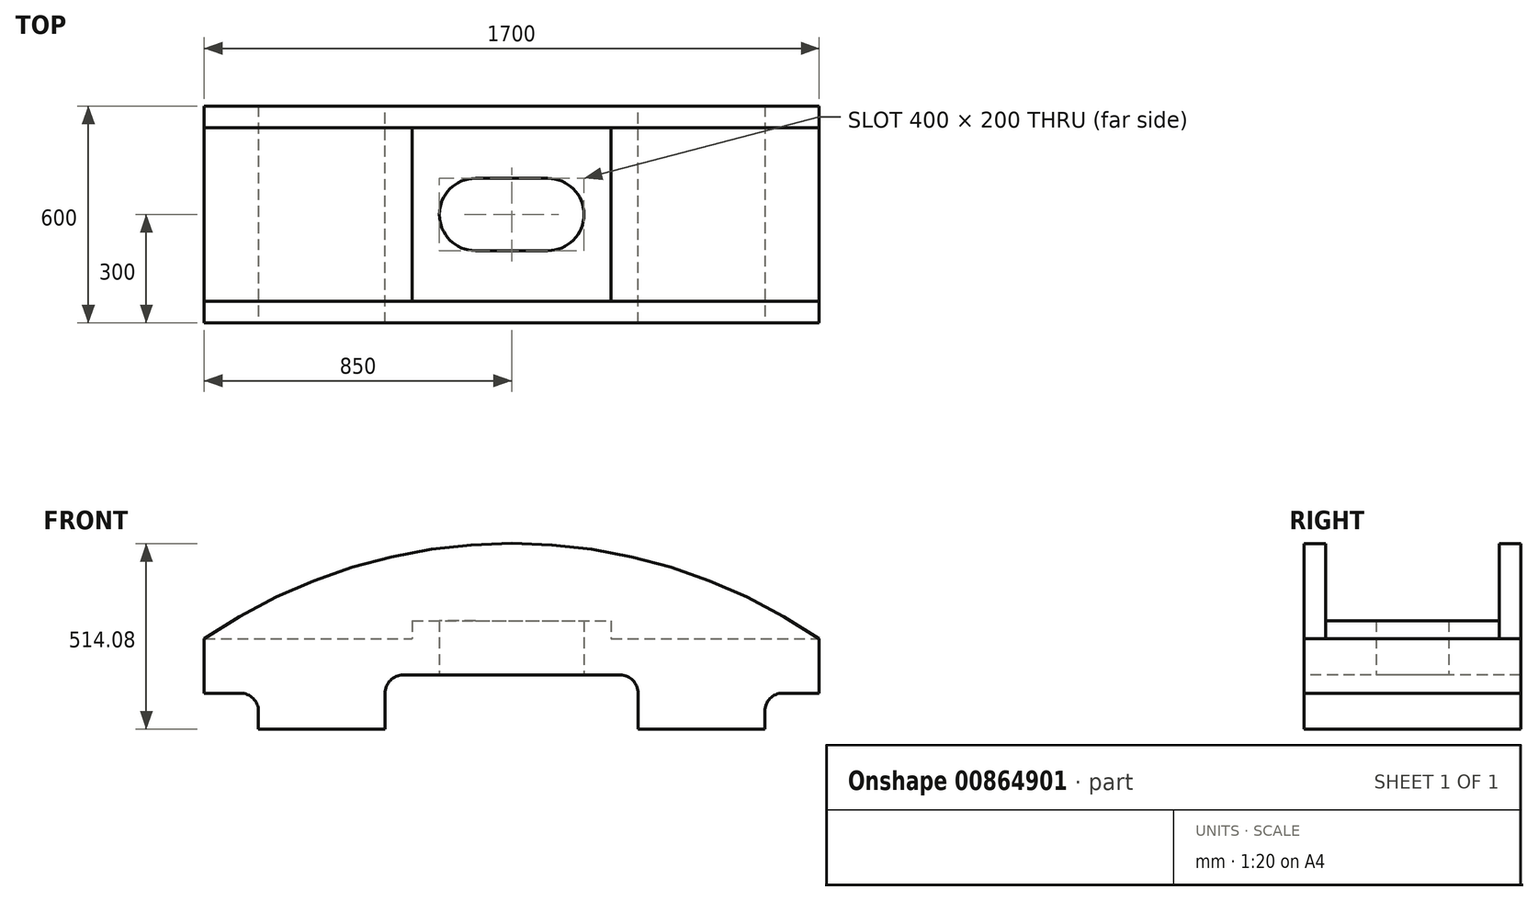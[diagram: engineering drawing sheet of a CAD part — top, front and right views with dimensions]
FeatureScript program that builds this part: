
annotation { "Feature Type Name" : "Feature", "Feature Type Description" : "" }
export const myFeature = defineFeature(function(context is Context, id is Id, definition is map)
    precondition{}
    {
        {
            var Q0;
            Q0=qCreatedBy(makeId("Front.planeOp"),FACE);
            var sketch = newSketch(context, id + "F0", { "sketchPlane" : qUnion([Q0])});
            skLineSegment(sketch, "E0.bottom", {"start": v(-850, -125) * mm, "end": v(850, -125) * mm});
            skLineSegment(sketch, "E0.top", {"start": v(-850, 125) * mm, "end": v(850, 125) * mm});
            skLineSegment(sketch, "E0.left", {"start": v(-850, -125) * mm, "end": v(-850, 125) * mm});
            skLineSegment(sketch, "E0.right", {"start": v(850, -125) * mm, "end": v(850, 125) * mm});
            skPoint(sketch, "E0.middle", {"position": v(0, 0) * mm});
            skLineSegment(sketch, "E1.bottom", {"start": v(-850, -125) * mm, "end": v(-700, -125) * mm});
            skLineSegment(sketch, "E1.top", {"start": v(-850, -25) * mm, "end": v(-700, -25) * mm});
            skLineSegment(sketch, "E1.left", {"start": v(-850, -125) * mm, "end": v(-850, -25) * mm});
            skLineSegment(sketch, "E1.right", {"start": v(-700, -125) * mm, "end": v(-700, -25) * mm});
            skSolve(sketch);
        }
        {
            var Q0;
            Q0 = qSketchRegion(id + "F0", true);
            extrude(context, id + "F1", {"entities" : qUnion([Q0]), "depth" : 600 * mm, "offsetDistance" : 25 * mm});
        }
        {
            var Q0;
            Q0=makeQuery(id+"F1.opExtrude","CAP_FACE",FACE,{"disambiguationData":[OSD([sQuery(id+"F0.wireOp",EDGE,"E0.bottom"),sQuery(id+"F0.wireOp",EDGE,"E0.top"),sQuery(id+"F0.wireOp",EDGE,"E0.left"),sQuery(id+"F0.wireOp",EDGE,"E0.right"),sQuery(id+"F0.wireOp",EDGE,"E1.bottom"),sQuery(id+"F0.wireOp",EDGE,"E1.left")])],"isStart":false});
            var sketch = newSketch(context, id + "F2", { "sketchPlane" : qUnion([Q0])});
            skLineSegment(sketch, "E2.bottom", {"start": v(-850, -125) * mm, "end": v(-700, -125) * mm});
            skLineSegment(sketch, "E2.top", {"start": v(-850, -25) * mm, "end": v(-700, -25) * mm});
            skLineSegment(sketch, "E2.left", {"start": v(-850, -125) * mm, "end": v(-850, -25) * mm});
            skLineSegment(sketch, "E2.right", {"start": v(-700, -125) * mm, "end": v(-700, -25) * mm});
            skSolve(sketch);
        }
        {
            var Q0;
            Q0 = qSketchRegion(id + "F2", true);
            extrude(context, id + "F3", {"entities" : qUnion([Q0]), "operationType" : NewBodyOperationType.REMOVE, "endBound" : BoundingType.THROUGH_ALL, "oppositeDirection" : true, "depth" : 25 * mm, "offsetDistance" : 25 * mm});
        }
        {
            var Q0;
            Q0=makeQuery(id+"F1.opExtrude","CAP_FACE",FACE,{"disambiguationData":[OSD([sQuery(id+"F0.wireOp",EDGE,"E0.bottom"),sQuery(id+"F0.wireOp",EDGE,"E0.top"),sQuery(id+"F0.wireOp",EDGE,"E0.left"),sQuery(id+"F0.wireOp",EDGE,"E0.right"),sQuery(id+"F0.wireOp",EDGE,"E1.bottom"),sQuery(id+"F0.wireOp",EDGE,"E1.left")])],"isStart":false});
            var sketch = newSketch(context, id + "F4", { "sketchPlane" : qUnion([Q0])});
            skLineSegment(sketch, "E3.bottom", {"start": v(850, -125) * mm, "end": v(700, -125) * mm});
            skLineSegment(sketch, "E3.top", {"start": v(850, -25) * mm, "end": v(700, -25) * mm});
            skLineSegment(sketch, "E3.left", {"start": v(850, -125) * mm, "end": v(850, -25) * mm});
            skLineSegment(sketch, "E3.right", {"start": v(700, -125) * mm, "end": v(700, -25) * mm});
            skSolve(sketch);
        }
        {
            var Q0;
            Q0 = qSketchRegion(id + "F4", true);
            extrude(context, id + "F5", {"entities" : qUnion([Q0]), "operationType" : NewBodyOperationType.REMOVE, "endBound" : BoundingType.THROUGH_ALL, "oppositeDirection" : true, "depth" : 25 * mm, "offsetDistance" : 25 * mm});
        }
        {
            var Q0;
            Q0=makeQuery(id+"F3.boolean.opBoolean","COPY",EDGE,{"derivedFrom":makeQuery(id+"F3.opExtrude","SWEPT_EDGE",EDGE,{"disambiguationData":[OSD([sQuery(id+"F2.wireOp",EDGE,"E2.top"),sQuery(id+"F2.wireOp",EDGE,"E2.right")])]})});
            fillet(context, id + "F6", {"entities" : qUnion([Q0]), "radius" : 50 * mm, "tangentPropagation" : true, "allowEdgeOverflow" : false});
        }
        {
            var Q0;
            Q0=makeQuery(id+"F5.boolean.opBoolean","COPY",EDGE,{"derivedFrom":makeQuery(id+"F5.opExtrude","SWEPT_EDGE",EDGE,{"disambiguationData":[OSD([sQuery(id+"F4.wireOp",EDGE,"E3.top"),sQuery(id+"F4.wireOp",EDGE,"E3.right")])]})});
            fillet(context, id + "F7", {"entities" : qUnion([Q0]), "radius" : 50 * mm, "tangentPropagation" : true, "allowEdgeOverflow" : false});
        }
        {
            var Q0;
            Q0=makeQuery(id+"F1.opExtrude","CAP_FACE",FACE,{"disambiguationData":[OSD([sQuery(id+"F0.wireOp",EDGE,"E0.bottom"),sQuery(id+"F0.wireOp",EDGE,"E0.top"),sQuery(id+"F0.wireOp",EDGE,"E0.left"),sQuery(id+"F0.wireOp",EDGE,"E0.right"),sQuery(id+"F0.wireOp",EDGE,"E1.bottom"),sQuery(id+"F0.wireOp",EDGE,"E1.left")])],"isStart":false});
            var sketch = newSketch(context, id + "F8", { "sketchPlane" : qUnion([Q0])});
            skArc(sketch, "E4", {"start": v(850, 125) * mm, "mid": v(0, 389.08) * mm, "end": v(-850, 125) * mm});
            skSolve(sketch);
        }
        {
            var Q0;
            Q0 = qSketchRegion(id + "F8", true);
            var Q1;
            Q1=makeQuery(id+"F8.imprint","IMPRINT",FACE,{"disambiguationData":[TD([[makeQuery(id+"F8.imprint","IMPRINT",EDGE,{"derivedFrom":sQuery(id+"F8.wireOp",EDGE,"E4")}),1.0]])]});
            extrude(context, id + "F9", {"entities" : qUnion([Q0, Q1]), "operationType" : NewBodyOperationType.ADD, "oppositeDirection" : true, "depth" : 60 * mm, "offsetDistance" : 25 * mm});
        }
        {
            var Q0;
            Q0=makeQuery(id+"F1.opExtrude","CAP_FACE",FACE,{"disambiguationData":[OSD([sQuery(id+"F0.wireOp",EDGE,"E0.bottom"),sQuery(id+"F0.wireOp",EDGE,"E0.top"),sQuery(id+"F0.wireOp",EDGE,"E0.left"),sQuery(id+"F0.wireOp",EDGE,"E0.right"),sQuery(id+"F0.wireOp",EDGE,"E1.bottom"),sQuery(id+"F0.wireOp",EDGE,"E1.left")])],"isStart":true});
            var sketch = newSketch(context, id + "F10", { "sketchPlane" : qUnion([Q0])});
            skArc(sketch, "E5", {"start": v(850, 125) * mm, "mid": v(0, 389.08) * mm, "end": v(-850, 125) * mm});
            skSolve(sketch);
        }
        {
            var Q0;
            Q0 = qSketchRegion(id + "F10", true);
            var Q1;
            Q1=makeQuery(id+"F10.imprint","IMPRINT",FACE,{"disambiguationData":[TD([[makeQuery(id+"F10.imprint","IMPRINT",EDGE,{"derivedFrom":sQuery(id+"F10.wireOp",EDGE,"E5")}),1.0]])]});
            extrude(context, id + "F11", {"entities" : qUnion([Q0, Q1]), "operationType" : NewBodyOperationType.ADD, "oppositeDirection" : true, "depth" : 60 * mm, "offsetDistance" : 25 * mm});
        }
        {
            var Q0;
            {var subQ0=sQuery(id+"F0.wireOp",EDGE,"E0.top");Q0=makeQuery(id+"F9.boolean.opBoolean","MERGE",FACE,{"derivedFrom":[makeQuery(id+"F1.opExtrude","CAP_FACE",FACE,{"disambiguationData":[OSD([sQuery(id+"F0.wireOp",EDGE,"E0.bottom"),subQ0,sQuery(id+"F0.wireOp",EDGE,"E0.left"),sQuery(id+"F0.wireOp",EDGE,"E0.right"),sQuery(id+"F0.wireOp",EDGE,"E1.bottom"),sQuery(id+"F0.wireOp",EDGE,"E1.left")])],"isStart":false}),makeQuery(id+"F9.opExtrude","CAP_FACE",FACE,{"disambiguationData":[OSD([subQ0,sQuery(id+"F8.wireOp",EDGE,"E4")])],"isStart":true})]});}
            var sketch = newSketch(context, id + "F12", { "sketchPlane" : qUnion([Q0])});
            skLineSegment(sketch, "E6.bottom", {"start": v(-350, -275) * mm, "end": v(350, -275) * mm});
            skLineSegment(sketch, "E6.top", {"start": v(-350, 25) * mm, "end": v(350, 25) * mm});
            skLineSegment(sketch, "E6.left", {"start": v(-350, -275) * mm, "end": v(-350, 25) * mm});
            skLineSegment(sketch, "E6.right", {"start": v(350, -275) * mm, "end": v(350, 25) * mm});
            skPoint(sketch, "E6.middle", {"position": v(0, -125) * mm});
            skSolve(sketch);
        }
        {
            var Q0;
            Q0 = qSketchRegion(id + "F12", true);
            extrude(context, id + "F13", {"entities" : qUnion([Q0]), "operationType" : NewBodyOperationType.REMOVE, "endBound" : BoundingType.THROUGH_ALL, "oppositeDirection" : true, "depth" : 25 * mm, "offsetDistance" : 25 * mm});
        }
        {
            var Q0;
            Q0=makeQuery(id+"F13.boolean.opBoolean","COPY",EDGE,{"derivedFrom":makeQuery(id+"F13.opExtrude","SWEPT_EDGE",EDGE,{"disambiguationData":[OSD([sQuery(id+"F12.wireOp",EDGE,"E6.top"),sQuery(id+"F12.wireOp",EDGE,"E6.right")])]})});
            fillet(context, id + "F14", {"entities" : qUnion([Q0]), "radius" : 50 * mm, "tangentPropagation" : true, "allowEdgeOverflow" : false});
        }
        {
            var Q0;
            Q0=makeQuery(id+"F13.boolean.opBoolean","COPY",EDGE,{"derivedFrom":makeQuery(id+"F13.opExtrude","SWEPT_EDGE",EDGE,{"disambiguationData":[OSD([sQuery(id+"F12.wireOp",EDGE,"E6.top"),sQuery(id+"F12.wireOp",EDGE,"E6.left")])]})});
            fillet(context, id + "F15", {"entities" : qUnion([Q0]), "radius" : 50 * mm, "tangentPropagation" : true, "allowEdgeOverflow" : false});
        }
        {
            var Q0;
            Q0=makeQuery(id+"F1.opExtrude","SWEPT_FACE",FACE,{"disambiguationData":[OSD([sQuery(id+"F0.wireOp",EDGE,"E0.top")])]});
            var sketch = newSketch(context, id + "F16", { "sketchPlane" : qUnion([Q0])});
            skLineSegment(sketch, "E7.bottom", {"start": v(-275, -540) * mm, "end": v(275, -540) * mm});
            skLineSegment(sketch, "E7.top", {"start": v(-275, -60) * mm, "end": v(275, -60) * mm});
            skLineSegment(sketch, "E7.left", {"start": v(-275, -540) * mm, "end": v(-275, -60) * mm});
            skLineSegment(sketch, "E7.right", {"start": v(275, -540) * mm, "end": v(275, -60) * mm});
            skPoint(sketch, "E7.middle", {"position": v(0, -300) * mm});
            skPoint(sketch, "E7.middle.positionSnap0", {"position": v(-850, -300) * mm});
            skPoint(sketch, "E7.centerSnap0", {"position": v(-850, -300) * mm});
            skLineSegment(sketch, "E8.bottom", {"start": v(-100, -400) * mm, "end": v(100, -400) * mm});
            skLineSegment(sketch, "E8.top", {"start": v(-100, -200) * mm, "end": v(100, -200) * mm});
            skLineSegment(sketch, "E8.left", {"start": v(-100, -400) * mm, "end": v(-100, -200) * mm});
            skLineSegment(sketch, "E8.right", {"start": v(100, -400) * mm, "end": v(100, -200) * mm});
            skCircle(sketch, "E9", {"center": v(-100, -300) * mm, "radius": 100 * mm});
            skCircle(sketch, "E10", {"center": v(100, -300) * mm, "radius": 100 * mm});
            skSolve(sketch);
        }
        {
            var Q0;
            Q0 = qSketchRegion(id + "F16", true);
            extrude(context, id + "F17", {"entities" : qUnion([Q0]), "operationType" : NewBodyOperationType.ADD, "depth" : 50 * mm, "offsetDistance" : 25 * mm});
        }
        {
            var Q0;
            Q0 = qSketchRegion(id + "F16", true);
            extrude(context, id + "F18", {"entities" : qUnion([Q0]), "operationType" : NewBodyOperationType.ADD, "depth" : 25 * mm, "offsetDistance" : 25 * mm});
        }
        {
            var Q0;
            Q0=makeQuery(id+"F17.boolean.opBoolean","SPLIT",FACE,{"disambiguationData":[TD([makeQuery(id+"F17.opExtrude","SWEPT_FACE",FACE,{"disambiguationData":[OSD([sQuery(id+"F16.wireOp",EDGE,"E8.bottom")])]})])],"derivedFrom":makeQuery(id+"F1.opExtrude","SWEPT_FACE",FACE,{"disambiguationData":[OSD([sQuery(id+"F0.wireOp",EDGE,"E0.top")])]})});
            extrude(context, id + "F19", {"entities" : qUnion([Q0]), "operationType" : NewBodyOperationType.REMOVE, "endBound" : BoundingType.THROUGH_ALL, "oppositeDirection" : true, "depth" : 25 * mm, "offsetDistance" : 25 * mm});
        }
    });
